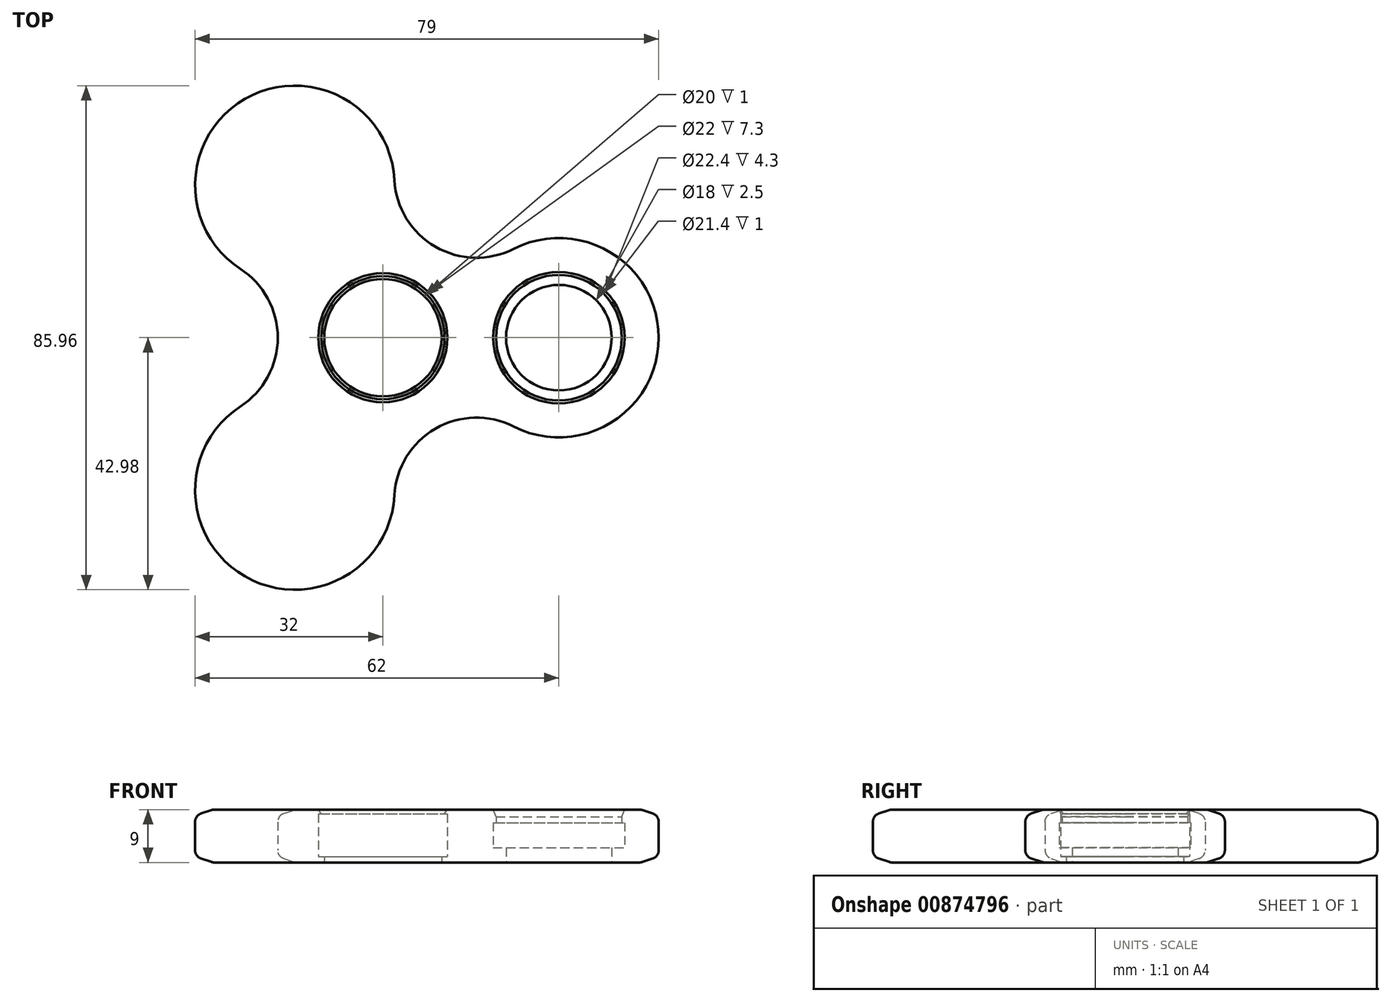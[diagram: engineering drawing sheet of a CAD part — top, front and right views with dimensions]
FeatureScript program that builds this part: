
annotation { "Feature Type Name" : "Feature", "Feature Type Description" : "" }
export const myFeature = defineFeature(function(context is Context, id is Id, definition is map)
    precondition{}
    {
        {
            var Q0;
            Q0=qCreatedBy(makeId("Top.planeOp"),FACE);
            var sketch = newSketch(context, id + "F0", { "sketchPlane" : qUnion([Q0])});
            skLineSegment(sketch, "E0", {"start": v(0, 0) * mm, "end": v(30, 0) * mm, "construction": true});
            skCircle(sketch, "E1", {"center": v(0, 0) * mm, "radius": 30 * mm, "construction": true});
            skLineSegment(sketch, "E2", {"start": v(0, 0) * mm, "end": v(-15, 25.98) * mm, "construction": true});
            skLineSegment(sketch, "E3", {"start": v(0, 0) * mm, "end": v(-15, -25.98) * mm, "construction": true});
            skArc(sketch, "E4", {"start": v(22.3, -15.16) * mm, "mid": v(47, 0) * mm, "end": v(22.3, 15.16) * mm});
            skArc(sketch, "E5", {"start": v(1.98, 26.89) * mm, "mid": v(-23.5, 40.7) * mm, "end": v(-24.27, 11.73) * mm});
            skArc(sketch, "E6", {"start": v(-24.27, -11.73) * mm, "mid": v(-23.5, -40.7) * mm, "end": v(1.98, -26.89) * mm});
            skArc(sketch, "E7", {"start": v(1.98, 26.89) * mm, "mid": v(8.96, 15.51) * mm, "end": v(22.3, 15.16) * mm});
            skArc(sketch, "E8.1.0", {"start": v(-24.27, -11.73) * mm, "mid": v(-17.91, 0) * mm, "end": v(-24.27, 11.73) * mm});
            skArc(sketch, "E8.2.0", {"start": v(22.3, -15.16) * mm, "mid": v(8.96, -15.51) * mm, "end": v(1.98, -26.89) * mm});
            skSolve(sketch);
        }
        {
            var Q0;
            Q0 = qSketchRegion(id + "F0", true);
            extrude(context, id + "F1", {"entities" : qUnion([Q0]), "depth" : 9 * mm, "offsetDistance" : 25 * mm});
        }
        {
            var Q0;
            Q0=qCreatedBy(makeId("Right.planeOp"),FACE);
            var sketch = newSketch(context, id + "F2", { "sketchPlane" : qUnion([Q0])});
            skLineSegment(sketch, "E9", {"start": v(0, 0) * mm, "end": v(0, 9) * mm});
            skLineSegment(sketch, "E10", {"start": v(0, 9) * mm, "end": v(11, 9) * mm});
            skLineSegment(sketch, "E11", {"start": v(11, 9) * mm, "end": v(10.5, 8.3) * mm});
            skLineSegment(sketch, "E12", {"start": v(10.5, 8.3) * mm, "end": v(11, 8.3) * mm});
            skLineSegment(sketch, "E13", {"start": v(11, 8.3) * mm, "end": v(11, 1) * mm});
            skLineSegment(sketch, "E14", {"start": v(11, 1) * mm, "end": v(10, 1) * mm});
            skLineSegment(sketch, "E15", {"start": v(10, 1) * mm, "end": v(10, 0) * mm});
            skLineSegment(sketch, "E16", {"start": v(10, 0) * mm, "end": v(0, 0) * mm});
            skLineSegment(sketch, "E17", {"start": v(0, 17.58) * mm, "end": v(0, -10.03) * mm, "construction": true});
            skSolve(sketch);
        }
        {
            var Q0;
            Q0 = qSketchRegion(id + "F2", true);
            var Q1;
            Q1=sQuery(id+"F2.wireOp",EDGE,"E17");
            revolve(context, id + "F3", {"operationType" : NewBodyOperationType.REMOVE, "surfaceOperationType" : NewSurfaceOperationType.NEW, "entities" : qUnion([Q0]), "axis" : qUnion([Q1]), "revolveType" : RevolveType.FULL, "oppositeDirection" : true});
        }
        {
            var Q0;
            Q0=qCreatedBy(makeId("Front.planeOp"),FACE);
            var sketch = newSketch(context, id + "F4", { "sketchPlane" : qUnion([Q0])});
            skLineSegment(sketch, "E18", {"start": v(30, 31.94) * mm, "end": v(30, -19.35) * mm, "construction": true});
            skLineSegment(sketch, "E19", {"start": v(30, 0) * mm, "end": v(30, 9) * mm});
            skLineSegment(sketch, "E20", {"start": v(30, 9) * mm, "end": v(18.8, 9) * mm});
            skLineSegment(sketch, "E21", {"start": v(19.3, 6.8) * mm, "end": v(18.8, 6.8) * mm});
            skLineSegment(sketch, "E22", {"start": v(18.8, 6.8) * mm, "end": v(18.8, 2.5) * mm});
            skLineSegment(sketch, "E23", {"start": v(18.8, 2.5) * mm, "end": v(21, 2.5) * mm});
            skLineSegment(sketch, "E24", {"start": v(21, 2.5) * mm, "end": v(21, 0) * mm});
            skLineSegment(sketch, "E25", {"start": v(21, 0) * mm, "end": v(30, 0) * mm});
            skLineSegment(sketch, "E26", {"start": v(19.3, 6.8) * mm, "end": v(19.3, 7.8) * mm});
            skLineSegment(sketch, "E27", {"start": v(19.3, 7.8) * mm, "end": v(18.8, 9) * mm});
            skSolve(sketch);
        }
        {
            var Q0;
            Q0 = qSketchRegion(id + "F4", true);
            var Q1;
            Q1=sQuery(id+"F4.wireOp",EDGE,"E18");
            revolve(context, id + "F5", {"operationType" : NewBodyOperationType.REMOVE, "surfaceOperationType" : NewSurfaceOperationType.NEW, "entities" : qUnion([Q0]), "axis" : qUnion([Q1]), "revolveType" : RevolveType.FULL, "oppositeDirection" : true});
        }
        {
            var Q0;
            Q0=makeQuery(id+"F1.opExtrude","CAP_EDGE",EDGE,{"disambiguationData":[OSD([sQuery(id+"F0.wireOp",EDGE,"E8.2.0")])],"isStart":false});
            var Q1;
            Q1=makeQuery(id+"F1.opExtrude","CAP_EDGE",EDGE,{"disambiguationData":[OSD([sQuery(id+"F0.wireOp",EDGE,"E8.2.0")])],"isStart":true});
            chamfer(context, id + "F6", {"entities" : qUnion([Q0, Q1]), "chamferType" : ChamferType.TWO_OFFSETS, "width1" : 3 * mm, "oppositeDirection" : false, "width2" : 1 * mm, "tangentPropagation" : true});
        }
        {
            var Q0;
            {var subQ0=sQuery(id+"F0.wireOp",EDGE,"E8.2.0");Q0=makeQuery(id+"F6.opChamfer","BLEND_EDGE",EDGE,{"blendedFrom":[makeQuery(id+"F1.opExtrude","CAP_EDGE",EDGE,{"disambiguationData":[OSD([subQ0])],"isStart":false}),makeQuery(id+"F1.opExtrude","CAP_FACE",FACE,{"disambiguationData":[OSD([sQuery(id+"F0.wireOp",EDGE,"E4"),sQuery(id+"F0.wireOp",EDGE,"E5"),sQuery(id+"F0.wireOp",EDGE,"E6"),sQuery(id+"F0.wireOp",EDGE,"E7"),sQuery(id+"F0.wireOp",EDGE,"E8.1.0"),subQ0])],"isStart":false})],"blendedInto":[makeQuery(id+"F1.opExtrude","CAP_FACE",FACE,{"disambiguationData":[OSD([sQuery(id+"F0.wireOp",EDGE,"E4"),sQuery(id+"F0.wireOp",EDGE,"E5"),sQuery(id+"F0.wireOp",EDGE,"E6"),sQuery(id+"F0.wireOp",EDGE,"E7"),sQuery(id+"F0.wireOp",EDGE,"E8.1.0"),subQ0])],"isStart":false})]});}
            var Q1;
            {var subQ0=sQuery(id+"F0.wireOp",EDGE,"E8.2.0");Q1=makeQuery(id+"F6.opChamfer","BLEND_EDGE",EDGE,{"blendedFrom":[makeQuery(id+"F1.opExtrude","CAP_EDGE",EDGE,{"disambiguationData":[OSD([subQ0])],"isStart":false}),makeQuery(id+"F1.opExtrude","SWEPT_FACE",FACE,{"disambiguationData":[OSD([subQ0])]})],"blendedInto":[makeQuery(id+"F1.opExtrude","SWEPT_FACE",FACE,{"disambiguationData":[OSD([subQ0])]})]});}
            var Q2;
            {var subQ0=sQuery(id+"F0.wireOp",EDGE,"E8.2.0");Q2=makeQuery(id+"F6.opChamfer","BLEND_EDGE",EDGE,{"blendedFrom":[makeQuery(id+"F1.opExtrude","CAP_EDGE",EDGE,{"disambiguationData":[OSD([subQ0])],"isStart":true}),makeQuery(id+"F1.opExtrude","SWEPT_FACE",FACE,{"disambiguationData":[OSD([subQ0])]})],"blendedInto":[makeQuery(id+"F1.opExtrude","SWEPT_FACE",FACE,{"disambiguationData":[OSD([subQ0])]})]});}
            var Q3;
            {var subQ0=sQuery(id+"F0.wireOp",EDGE,"E8.2.0");Q3=makeQuery(id+"F6.opChamfer","BLEND_EDGE",EDGE,{"blendedFrom":[makeQuery(id+"F1.opExtrude","CAP_EDGE",EDGE,{"disambiguationData":[OSD([subQ0])],"isStart":true}),makeQuery(id+"F1.opExtrude","CAP_FACE",FACE,{"disambiguationData":[OSD([sQuery(id+"F0.wireOp",EDGE,"E4"),sQuery(id+"F0.wireOp",EDGE,"E5"),sQuery(id+"F0.wireOp",EDGE,"E6"),sQuery(id+"F0.wireOp",EDGE,"E7"),sQuery(id+"F0.wireOp",EDGE,"E8.1.0"),subQ0])],"isStart":true})],"blendedInto":[makeQuery(id+"F1.opExtrude","CAP_FACE",FACE,{"disambiguationData":[OSD([sQuery(id+"F0.wireOp",EDGE,"E4"),sQuery(id+"F0.wireOp",EDGE,"E5"),sQuery(id+"F0.wireOp",EDGE,"E6"),sQuery(id+"F0.wireOp",EDGE,"E7"),sQuery(id+"F0.wireOp",EDGE,"E8.1.0"),subQ0])],"isStart":true})]});}
            fillet(context, id + "F7", {"entities" : qUnion([Q0, Q1, Q2, Q3]), "radius" : 1.5 * mm, "tangentPropagation" : true, "allowEdgeOverflow" : false});
        }
    });
